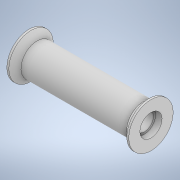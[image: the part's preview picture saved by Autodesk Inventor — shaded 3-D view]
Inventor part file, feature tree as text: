
AUTODESK INVENTOR PART (.ipt)
format: ipt  version: 2021 (Build 250183000, 183)  size: 124,416 bytes
history: native  units: mm
features: revolve x1, sketch x1
ambient origin geometry x8: Origin, YZ Plane, XZ Plane, XY Plane, X Axis, Y Axis, Z Axis, Center Point
bodies: Solid1 (feature_tree)
feature tree (2):
  revolve  "Revolution1"  [1 undecoded]
  sketch  "Sketch1"  dims[d0=11.0mm d1=6.5mm d2=9.0mm d4=105.0mm d6=2.0mm d7=16.0mm d8=22.0mm d9=90.0deg]
note: 1 required parameter value undecoded (feature->parameter linkage not recoverable at this tier; creation-order binding heuristic only, values carry confidence <= 0.55)
